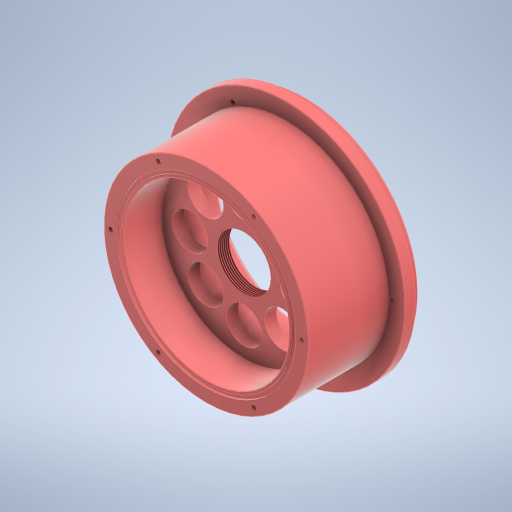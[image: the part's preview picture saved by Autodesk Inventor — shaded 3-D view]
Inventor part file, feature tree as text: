
AUTODESK INVENTOR PART (.ipt)
format: ipt  version: 2023 (Build 270158000, 158)  size: 501,248 bytes
history: native  units: mm
features: sketch x6, chamfer x3, hole x3, pattern_circular x3, extrude x2, revolve x1, plane x1, projected_geometry x1
ambient origin geometry x8: Origin, YZ Plane, XZ Plane, XY Plane, X Axis, Y Axis, Z Axis, Center Point
bodies: Solid1 (feature_tree)
feature tree (20):
  revolve  "Revolution1"  [1 undecoded]
  chamfer  "Chamfer4"  Distance=30.0mm Angle=360.0deg
  hole  "Hole1"  [1 undecoded]
  pattern_circular  "Circular Pattern1"  [2 undecoded]
  chamfer  "Chamfer5"  Distance=2.0mm Angle=45.0deg
  hole  "Hole2"  [1 undecoded]
  pattern_circular  "Circular Pattern2"  Count=5  [1 undecoded]
  plane  "Work Plane1"
  chamfer  "Chamfer6"  Distance=10.0mm
  extrude  "Extrusion3"  Depth=60.0mm TaperAngle=360.0deg
  pattern_circular  "Circular Pattern3"  Angle=45.0deg  [1 undecoded]
  hole  "Hole4"  [1 undecoded]
  extrude  "Extrusion4"  Depth=1.23mm
  sketch  "Sketch1"  dims[d2=4.6mm d3=10.0mm]
  sketch  "Sketch2"  dims[d8=88.9mm]
  sketch  "Sketch3"  dims[d9=120.0mm]
  projected_geometry  "Projected Loop1"
  sketch  "Sketch7"  dims[d10=360.0deg]
  sketch  "Sketch8"  dims[d20=114.0mm]
  sketch  "Sketch9"  dims[d26=53.0mm d27=2.459mm d28=15.0mm d29=4.0mm d30=4.6mm d31=90.0deg d32=8.0mm d33=20.594885mm d34=30.0mm d35=360.0deg d37=1.0mm d38=2.0mm d39=4.363323mm d40=2.0mm d41=3.0mm d42=2.0mm d43=45.0deg d44=83.0mm d45=50.0mm d46=10.0mm d47=2.459mm d48=6.0mm d49=6.3mm d50=2.0mm d51=90.0deg d52=8.8mm d53=20.594885mm d54=60.0mm d55=360.0deg d61=0.25mm d62=2.0mm d63=45.0deg d65=48.0mm d68=86.0mm d69=2.0mm d70=1.2mm d81=6.0mm d82=25.0mm d83=26.0mm d84=18.0mm d85=10.0mm d86=0.0mm d87=80.0mm d88=360.0deg d90=26.917468mm d91=56.0mm d92=3.6mm d93=2.0mm d94=90.0deg d95=8.0mm d96=20.594885mm d97=86.0mm d98=2.0mm d99=1.23mm d100=0.0mm]
note: 8 required parameter values undecoded (feature->parameter linkage not recoverable at this tier; creation-order binding heuristic only, values carry confidence <= 0.55)